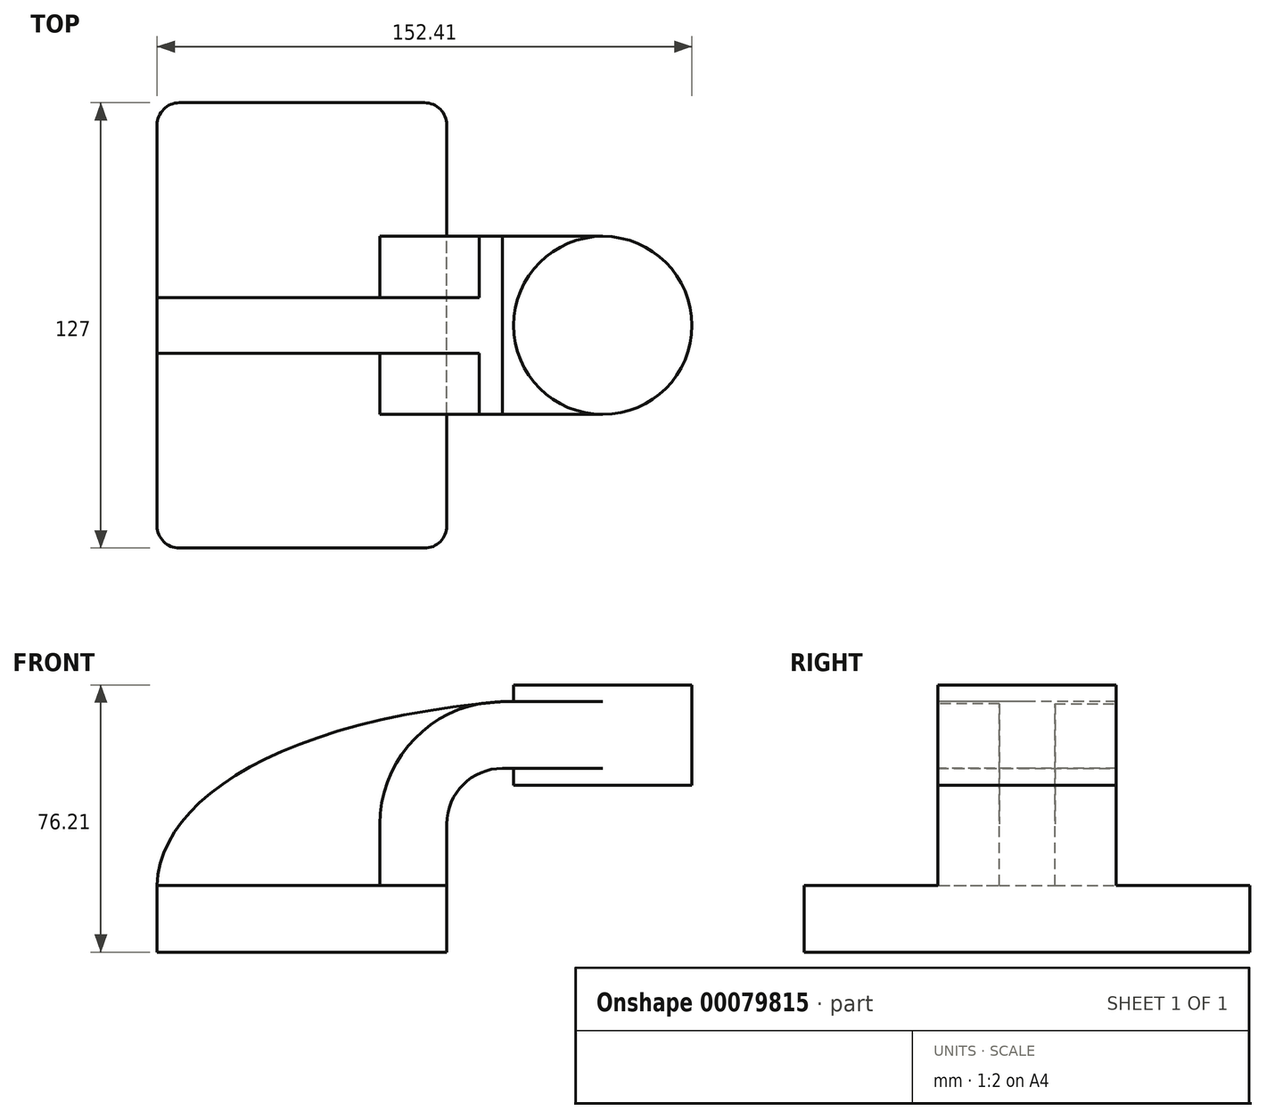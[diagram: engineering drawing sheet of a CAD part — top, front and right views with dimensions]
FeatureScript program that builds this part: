
annotation { "Feature Type Name" : "Feature", "Feature Type Description" : "" }
export const myFeature = defineFeature(function(context is Context, id is Id, definition is map)
    precondition{}
    {
        {
            var Q0;
            Q0=qCreatedBy(makeId("Front.planeOp"),FACE);
            var sketch = newSketch(context, id + "F0", { "sketchPlane" : qUnion([Q0])});
            skLineSegment(sketch, "E0.bottom", {"start": v(-41.28, 9.52) * mm, "end": v(41.27, 9.53) * mm});
            skLineSegment(sketch, "E0.top", {"start": v(-41.28, -9.53) * mm, "end": v(41.28, -9.53) * mm});
            skLineSegment(sketch, "E0.left", {"start": v(-41.28, 9.52) * mm, "end": v(-41.28, -9.53) * mm});
            skLineSegment(sketch, "E0.right", {"start": v(41.27, 9.53) * mm, "end": v(41.28, -9.52) * mm});
            skPoint(sketch, "E0.middle", {"position": v(0, 0) * mm});
            skLineSegment(sketch, "E1.bottom", {"start": v(60.32, 38.1) * mm, "end": v(111.12, 38.1) * mm});
            skLineSegment(sketch, "E1.top", {"start": v(60.32, 66.68) * mm, "end": v(111.12, 66.68) * mm});
            skLineSegment(sketch, "E1.left", {"start": v(60.32, 38.1) * mm, "end": v(60.32, 66.68) * mm});
            skLineSegment(sketch, "E1.right", {"start": v(111.12, 38.1) * mm, "end": v(111.12, 66.68) * mm});
            skPoint(sketch, "E1.middle", {"position": v(85.72, 52.39) * mm});
            skLineSegment(sketch, "E2", {"start": v(41.27, 9.53) * mm, "end": v(41.27, 27) * mm});
            skArc(sketch, "E3", {"start": v(41.27, 27) * mm, "mid": v(45.92, 38.23) * mm, "end": v(57.15, 42.88) * mm});
            skLineSegment(sketch, "E4", {"start": v(57.15, 42.88) * mm, "end": v(85.72, 42.88) * mm});
            skArc(sketch, "E5.0", {"start": v(53.97, 27) * mm, "mid": v(54.9, 29.25) * mm, "end": v(57.15, 30.18) * mm});
            skLineSegment(sketch, "E6.0", {"start": v(57.15, 61.93) * mm, "end": v(85.72, 61.93) * mm});
            skArc(sketch, "E6.1", {"start": v(22.22, 27) * mm, "mid": v(32.45, 51.7) * mm, "end": v(57.15, 61.93) * mm});
            skLineSegment(sketch, "E6.2", {"start": v(22.22, 9.53) * mm, "end": v(22.22, 27) * mm});
            skLineSegment(sketch, "E7", {"start": v(85.72, 38.1) * mm, "end": v(85.72, 66.68) * mm});
            skFitSpline(sketch, "E8", {"points": [v(-41.28, 9.52) * mm, v(57.15, 61.93) * mm], "startDerivative": vector(1.73, 74.45) * mm, "endDerivative": vector(186.53, 15.86) * mm});
            skSolve(sketch);
        }
        {
            var Q0;
            Q0=makeQuery(id+"F0.imprint","IMPRINT",FACE,{"disambiguationData":[TD([[makeQuery(id+"F0.imprint","IMPRINT",EDGE,{"derivedFrom":sQuery(id+"F0.wireOp",EDGE,"E0.top")}),1.0]])]});
            extrude(context, id + "F1", {"entities" : qUnion([Q0]), "endBound" : BoundingType.SYMMETRIC, "depth" : 127 * mm});
        }
        {
            var Q0;
            {var subQ1=sQuery(id+"F0.wireOp",EDGE,"E2");Q0=makeQuery(id+"F0.imprint","IMPRINT",FACE,{"disambiguationData":[TD([[makeQuery(id+"F0.imprint","IMPRINT",EDGE,{"derivedFrom":subQ1}),1.0]])]});}
            var Q1;
            {var subQ0=sQuery(id+"F0.wireOp",EDGE,"E4");var subQ1=sQuery(id+"F0.wireOp",EDGE,"E1.left");var subQ2=makeQuery(id+"F0.imprint","INTERSECT",VERTEX,{"derivedFrom":[subQ1,subQ0]});Q1=makeQuery(id+"F0.imprint","IMPRINT",FACE,{"disambiguationData":[TD([[makeQuery(id+"F0.imprint","IMPRINT",EDGE,{"disambiguationData":[TD([[subQ2,-1.0]])],"derivedFrom":subQ1}),-1.0]])]});}
            extrude(context, id + "F2", {"entities" : qUnion([Q0, Q1]), "operationType" : NewBodyOperationType.ADD, "endBound" : BoundingType.SYMMETRIC, "depth" : 50.8 * mm});
        }
        {
            var Q0;
            {var subQ3=sQuery(id+"F0.wireOp",EDGE,"E6.2");Q0=makeQuery(id+"F0.imprint","IMPRINT",FACE,{"disambiguationData":[TD([[makeQuery(id+"F0.imprint","IMPRINT",EDGE,{"derivedFrom":subQ3}),1.0]])]});}
            extrude(context, id + "F3", {"entities" : qUnion([Q0]), "operationType" : NewBodyOperationType.ADD, "endBound" : BoundingType.SYMMETRIC, "depth" : 15.88 * mm});
        }
        {
            var Q0;
            {var subQ0=sQuery(id+"F0.wireOp",EDGE,"E1.right");Q0=makeQuery(id+"F0.imprint","IMPRINT",FACE,{"disambiguationData":[TD([[makeQuery(id+"F0.imprint","IMPRINT",EDGE,{"derivedFrom":subQ0}),1.0]])]});}
            var Q1;
            Q1=sQuery(id+"F0.wireOp",EDGE,"E7");
            revolve(context, id + "F4", {"operationType" : NewBodyOperationType.ADD, "entities" : qUnion([Q0]), "axis" : qUnion([Q1]), "revolveType" : RevolveType.FULL});
        }
        {
            var Q0;
            Q0=makeQuery(id+"F1.opExtrude","CAP_EDGE",EDGE,{"disambiguationData":[OSD([sQuery(id+"F0.wireOp",EDGE,"E0.right")])],"isStart":false});
            var Q1;
            Q1=makeQuery(id+"F1.opExtrude","CAP_EDGE",EDGE,{"disambiguationData":[OSD([sQuery(id+"F0.wireOp",EDGE,"E0.left")])],"isStart":false});
            var Q2;
            Q2=makeQuery(id+"F1.opExtrude","CAP_EDGE",EDGE,{"disambiguationData":[OSD([sQuery(id+"F0.wireOp",EDGE,"E0.right")])],"isStart":true});
            var Q3;
            Q3=makeQuery(id+"F1.opExtrude","CAP_EDGE",EDGE,{"disambiguationData":[OSD([sQuery(id+"F0.wireOp",EDGE,"E0.left")])],"isStart":true});
            fillet(context, id + "F5", {"entities" : qUnion([Q0, Q1, Q2, Q3]), "radius" : 6.35 * mm, "tangentPropagation" : true, "allowEdgeOverflow" : false});
        }
    });
